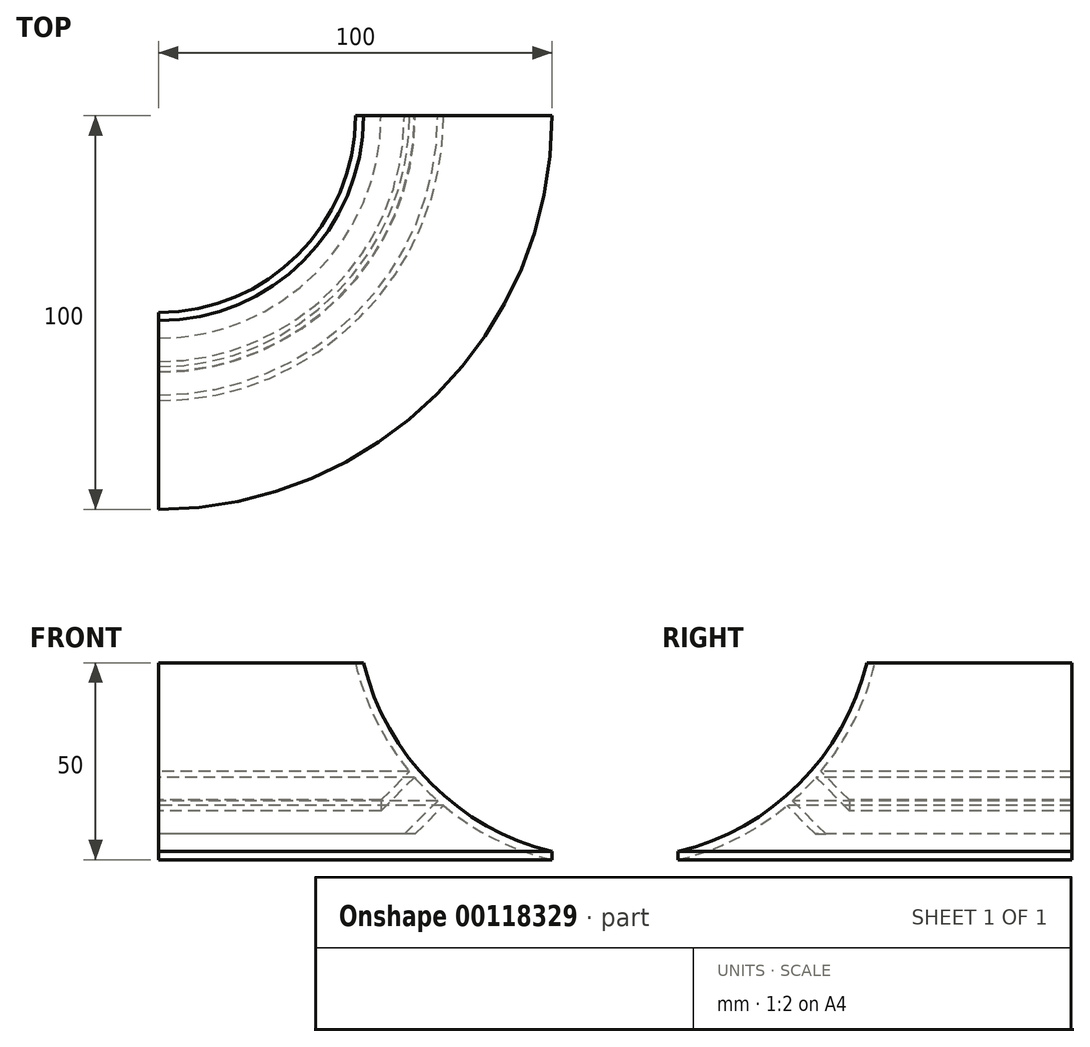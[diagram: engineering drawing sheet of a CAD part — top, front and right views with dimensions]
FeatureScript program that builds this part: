
annotation { "Feature Type Name" : "Feature", "Feature Type Description" : "" }
export const myFeature = defineFeature(function(context is Context, id is Id, definition is map)
    precondition{}
    {
        {
            var Q0;
            Q0=qCreatedBy(makeId("Top.planeOp"),FACE);
            var sketch = newSketch(context, id + "F0", { "sketchPlane" : qUnion([Q0])});
            skArc(sketch, "E0", {"start": v(0, 0) * mm, "mid": v(35.36, 14.64) * mm, "end": v(50, 50) * mm});
            skLineSegment(sketch, "E1", {"start": v(0, 0) * mm, "end": v(0, -50) * mm});
            skArc(sketch, "E2", {"start": v(0, -50) * mm, "mid": v(70.71, -20.71) * mm, "end": v(100, 50) * mm});
            skLineSegment(sketch, "E3", {"start": v(50, 50) * mm, "end": v(100, 50) * mm});
            skSolve(sketch);
        }
        {
            var Q0;
            Q0=qCreatedBy(makeId("Right.planeOp"),FACE);
            var sketch = newSketch(context, id + "F1", { "sketchPlane" : qUnion([Q0])});
            skArc(sketch, "E4", {"start": v(-50, 0) * mm, "mid": v(-17.87, 17.87) * mm, "end": v(0, 50) * mm});
            skLineSegment(sketch, "E5", {"start": v(0, 0) * mm, "end": v(-50, 0) * mm});
            skLineSegment(sketch, "E6", {"start": v(-50, 0) * mm, "end": v(-42.79, 0) * mm});
            skLineSegment(sketch, "E7", {"start": v(0, 50) * mm, "end": v(0, 0) * mm});
            skLineSegment(sketch, "E8", {"start": v(-50, 0) * mm, "end": v(-50, 50) * mm});
            skLineSegment(sketch, "E9", {"start": v(-50, 50) * mm, "end": v(0, 50) * mm});
            skPoint(sketch, "E10", {"position": v(-17.87, 17.87) * mm});
            skLineSegment(sketch, "E11", {"start": v(-17.87, 17.87) * mm, "end": v(-9.47, 9.47) * mm});
            skLineSegment(sketch, "E12", {"start": v(-12.44, 6.5) * mm, "end": v(-9.47, 9.47) * mm});
            skLineSegment(sketch, "E13", {"start": v(-12.44, 6.5) * mm, "end": v(-20.93, 15) * mm});
            skLineSegment(sketch, "E14", {"start": v(-15.14, 6.5) * mm, "end": v(-22.38, 13.74) * mm});
            skLineSegment(sketch, "E15", {"start": v(-15.14, 6.5) * mm, "end": v(-12.44, 6.5) * mm});
            skLineSegment(sketch, "E16.MirrorCS", {"start": v(-6.5, 12.44) * mm, "end": v(-15, 20.93) * mm});
            skLineSegment(sketch, "E17.MirrorCS", {"start": v(-6.5, 15.14) * mm, "end": v(-13.74, 22.38) * mm});
            skLineSegment(sketch, "E18.MirrorCS", {"start": v(-6.5, 15.14) * mm, "end": v(-6.5, 12.44) * mm});
            skArc(sketch, "E19.0", {"start": v(-50.46, 1.95) * mm, "mid": v(-19.28, 19.28) * mm, "end": v(-1.95, 50.46) * mm});
            skSolve(sketch);
        }
        {
            var Q0;
            Q0=qCreatedBy(makeId("Front.planeOp"),FACE);
            cPlane(context, id + "F2", {"entities" : qUnion([Q0]), "cplaneType" : CPlaneType.OFFSET, "offset" : 50 * mm, "oppositeDirection" : true, "width" : 150 * mm, "height" : 150 * mm});
        }
        {
            var Q0;
            Q0=qCreatedBy(id+"F2.planeOp",FACE);
            var sketch = newSketch(context, id + "F3", { "sketchPlane" : qUnion([Q0])});
            skLineSegment(sketch, "E20", {"start": v(50, 0) * mm, "end": v(50, 50) * mm});
            skArc(sketch, "E21", {"start": v(50, 50) * mm, "mid": v(67.87, 17.87) * mm, "end": v(100, 0) * mm});
            skLineSegment(sketch, "E22", {"start": v(100, 0) * mm, "end": v(50, 0) * mm});
            skLineSegment(sketch, "E23", {"start": v(0, 0) * mm, "end": v(0, 56.71) * mm});
            skSolve(sketch);
        }
        {
            var Q0;
            {var subQ0=sQuery(id+"F1.wireOp",EDGE,"loLzpiYG-LPMr-jdzZ-KjVN-8gdMNQGE42KB");Q0=makeQuery(id+"F1.imprint","IMPRINT",FACE,{"disambiguationData":[TD([[makeQuery(id+"F1.imprint","IMPRINT",EDGE,{"derivedFrom":subQ0}),-1.0]])]});}
            var Q1;
            {var subQ0=sQuery(id+"F1.wireOp",EDGE,"kw3RAWpF-j8sq-xCaJ-oxBF-Hq4lyIRaCmmW");Q1=makeQuery(id+"F1.imprint","IMPRINT",FACE,{"disambiguationData":[TD([[makeQuery(id+"F1.imprint","IMPRINT",EDGE,{"derivedFrom":subQ0}),1.0]])]});}
            var Q2;
            {var subQ0=sQuery(id+"F1.wireOp",EDGE,"E4");var subQ3=makeQuery(id+"F1.imprint","INTERSECT",VERTEX,{"derivedFrom":[subQ0,sQuery(id+"F1.wireOp",EDGE,"E13")]});Q2=makeQuery(id+"F1.imprint","IMPRINT",FACE,{"disambiguationData":[TD([[makeQuery(id+"F1.imprint","IMPRINT",EDGE,{"disambiguationData":[TD([[subQ3,1.0]])],"derivedFrom":subQ0}),1.0]])]});}
            var Q3;
            {var subQ0=sQuery(id+"F1.wireOp",EDGE,"E13");Q3=makeQuery(id+"F1.imprint","IMPRINT",FACE,{"disambiguationData":[TD([[makeQuery(id+"F1.imprint","IMPRINT",EDGE,{"derivedFrom":subQ0}),1.0]])]});}
            var Q4;
            {var subQ0=sQuery(id+"F1.wireOp",EDGE,"E16.MirrorCS");Q4=makeQuery(id+"F1.imprint","IMPRINT",FACE,{"disambiguationData":[TD([[makeQuery(id+"F1.imprint","IMPRINT",EDGE,{"derivedFrom":subQ0}),-1.0]])]});}
            var Q5;
            Q5=sQuery(id+"F3.wireOp",EDGE,"E23");
            revolve(context, id + "F4", {"entities" : qUnion([Q0, Q1, Q2, Q3, Q4]), "axis" : qUnion([Q5]), "revolveType" : RevolveType.ONE_DIRECTION, "angle" : 90 * degree});
        }
    });
